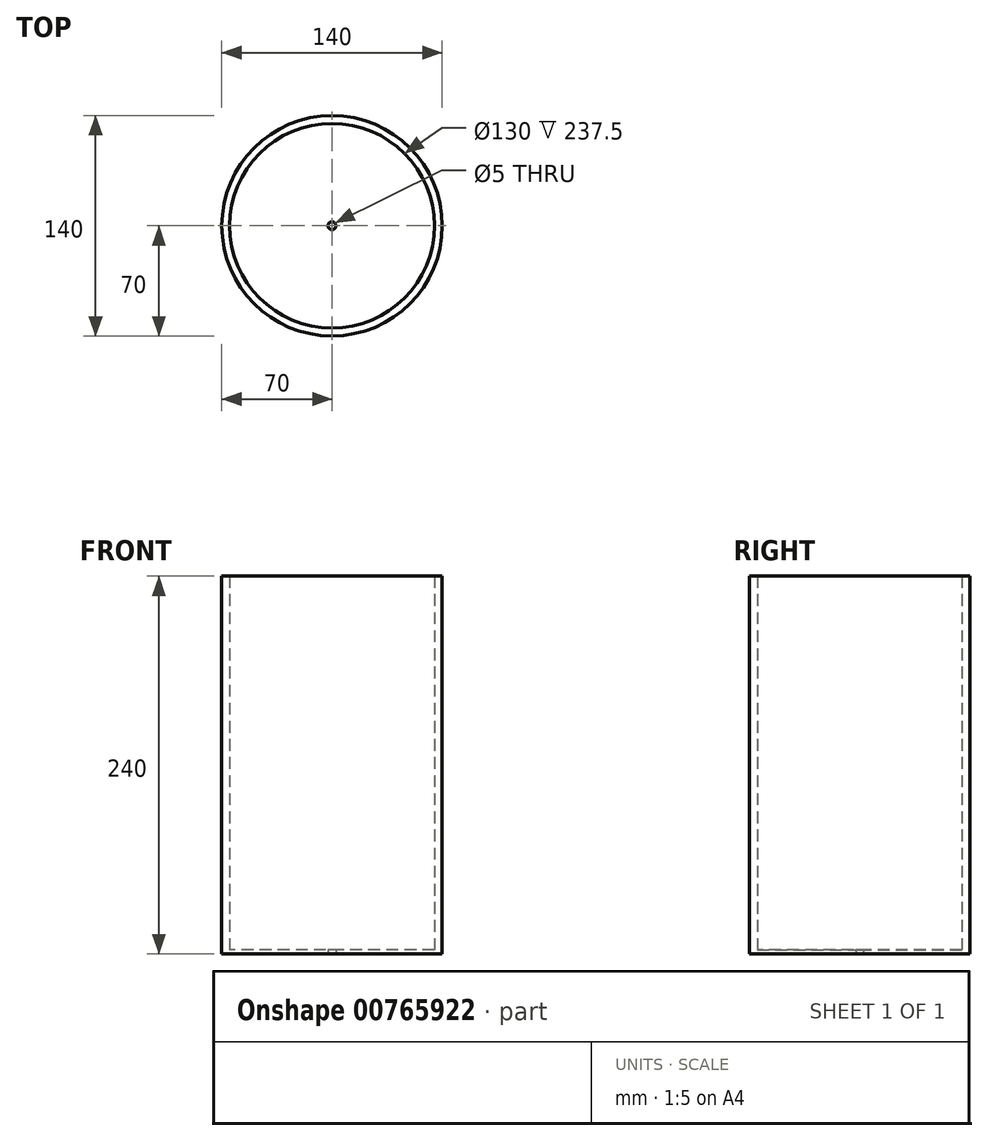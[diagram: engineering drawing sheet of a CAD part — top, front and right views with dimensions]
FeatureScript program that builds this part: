
annotation { "Feature Type Name" : "Feature", "Feature Type Description" : "" }
export const myFeature = defineFeature(function(context is Context, id is Id, definition is map)
    precondition{}
    {
        {
            var Q0;
            Q0=qCreatedBy(makeId("Top.planeOp"),FACE);
            var sketch = newSketch(context, id + "F0", { "sketchPlane" : qUnion([Q0])});
            skLineSegment(sketch, "E0.bottom", {"start": v(-70, 70) * mm, "end": v(70, 70) * mm});
            skLineSegment(sketch, "E0.top", {"start": v(-70, -70) * mm, "end": v(70, -70) * mm});
            skLineSegment(sketch, "E0.left", {"start": v(-70, 70) * mm, "end": v(-70, -70) * mm});
            skLineSegment(sketch, "E0.right", {"start": v(70, 70) * mm, "end": v(70, -70) * mm});
            skPoint(sketch, "E0.middle", {"position": v(0, 0) * mm});
            skCircle(sketch, "E1", {"center": v(0, 0) * mm, "radius": 70 * mm});
            skCircle(sketch, "E2", {"center": v(0, 0) * mm, "radius": 65 * mm});
            skCircle(sketch, "E3", {"center": v(0, 0) * mm, "radius": 1.25 * mm});
            skSolve(sketch);
        }
        {
            var Q0;
            Q0=makeQuery(id+"F0.imprint","IMPRINT",FACE,{"disambiguationData":[TD([[makeQuery(id+"F0.imprint","IMPRINT",EDGE,{"derivedFrom":sQuery(id+"F0.wireOp",EDGE,"E2")}),-1.0]])]});
            extrude(context, id + "F1", {"entities" : qUnion([Q0]), "depth" : 240 * mm, "offsetDistance" : 25.4 * mm});
        }
        {
            var Q0;
            Q0=makeQuery(id+"F0.imprint","IMPRINT",FACE,{"disambiguationData":[TD([[makeQuery(id+"F0.imprint","IMPRINT",EDGE,{"derivedFrom":sQuery(id+"F0.wireOp",EDGE,"E2")}),1.0]])]});
            var Q1;
            Q1=sQuery(id+"F0.wireOp",EDGE,"E1");
            extrude(context, id + "F2", {"entities" : qUnion([Q0]), "operationType" : NewBodyOperationType.ADD, "surfaceEntities" : qUnion([Q1]), "depth" : 2.5 * mm, "offsetDistance" : 25.4 * mm});
        }
        {
            var Q0;
            Q0=sQuery(id+"F0.wireOp",VERTEX,"E0.middle");
            var Q1;
            Q1=makeQuery(id+"F1.opExtrude","SWEPT_BODY",BODY,{"disambiguationData":[OSD([sQuery(id+"F0.wireOp",EDGE,"E1"),sQuery(id+"F0.wireOp",EDGE,"E2")])]});
            hole(context, id + "F3", {"style" : HoleStyle.SIMPLE, "endStyle" : HoleEndStyle.THROUGH, "oppositeDirection" : true, "holeDiameter" : 5 * mm, "majorDiameter" : 6.35 * mm, "isTappedThrough" : true, "tappedDepth" : 12.7 * mm, "tapClearance" : 3, "locations" : qUnion([Q0]), "scope" : qUnion([Q1])});
        }
    });
